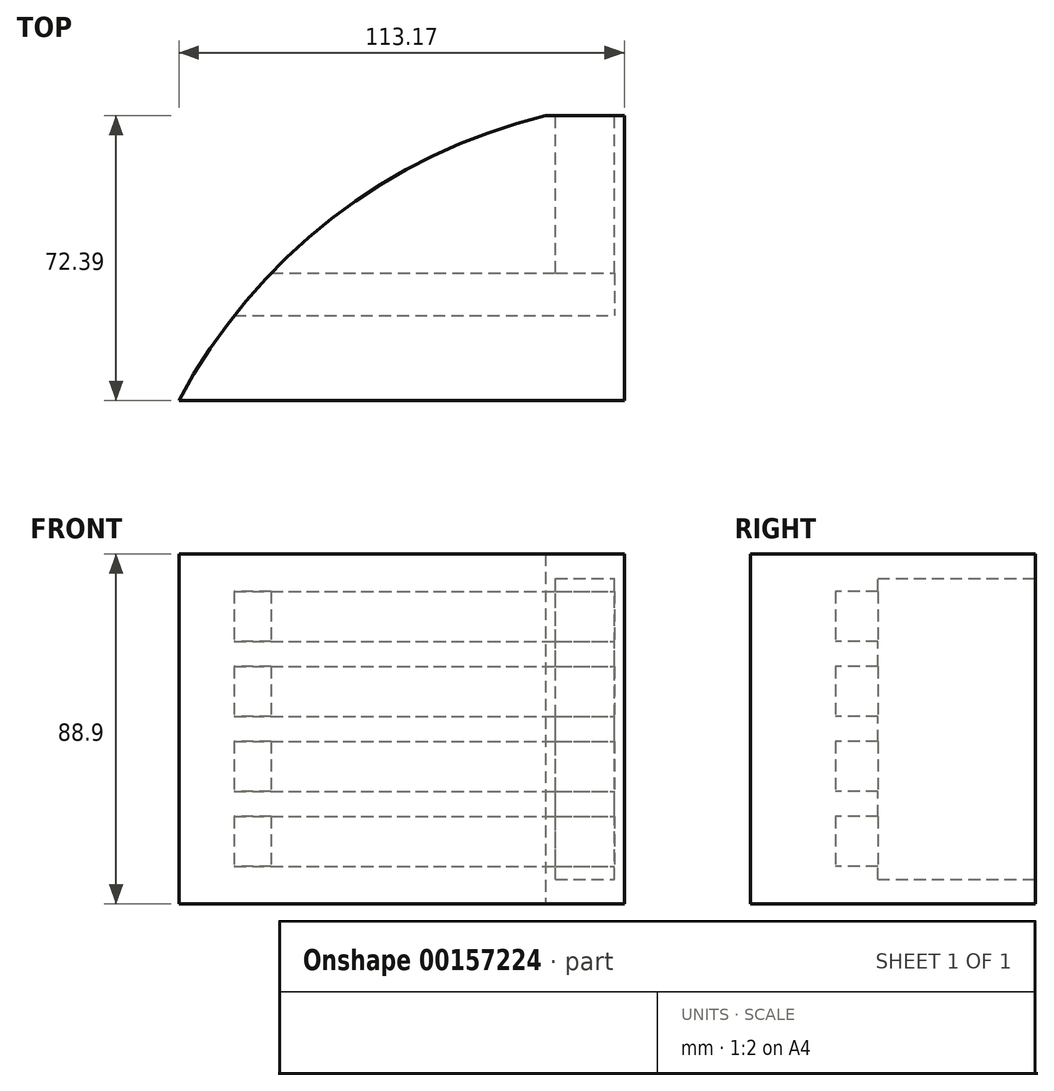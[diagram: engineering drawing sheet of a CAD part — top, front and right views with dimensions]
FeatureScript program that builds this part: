
annotation { "Feature Type Name" : "Feature", "Feature Type Description" : "" }
export const myFeature = defineFeature(function(context is Context, id is Id, definition is map)
    precondition{}
    {
        {
            var Q0;
            Q0=qCreatedBy(makeId("Top.planeOp"),FACE);
            var sketch = newSketch(context, id + "F0", { "sketchPlane" : qUnion([Q0])});
            skLineSegment(sketch, "E0", {"start": v(-50.05, -32.21) * mm, "end": v(43.12, -32.21) * mm});
            skLineSegment(sketch, "E1", {"start": v(43.12, -32.21) * mm, "end": v(43.12, 40.18) * mm});
            skArc(sketch, "E2", {"start": v(43.12, 40.18) * mm, "mid": v(-11.24, 14) * mm, "end": v(-50.05, -32.21) * mm});
            skSolve(sketch);
        }
        {
            var Q0;
            Q0 = qSketchRegion(id + "F0", true);
            extrude(context, id + "F1", {"entities" : qUnion([Q0]), "depth" : 88.9 * mm});
        }
        {
            var Q0;
            Q0=makeQuery(id+"F1.opExtrude","SWEPT_FACE",FACE,{"disambiguationData":[OSD([sQuery(id+"F0.wireOp",EDGE,"E1")])]});
            var sketch = newSketch(context, id + "F2", { "sketchPlane" : qUnion([Q0])});
            skSolve(sketch);
        }
        {
            var Q0;
            {var subQ0=sQuery(id+"F0.wireOp",EDGE,"E1");Q0=makeQuery(id+"F2.imprint","IMPRINT",FACE,{"disambiguationData":[TD([[makeQuery(id+"F2.imprint","IMPRINT",EDGE,{"derivedFrom":makeQuery(id+"F1.opExtrude","CAP_EDGE",EDGE,{"disambiguationData":[OSD([subQ0])],"isStart":true})}),1.0]])]});}
            var sketch = newSketch(context, id + "F3", { "sketchPlane" : qUnion([Q0])});
            skPoint(sketch, "E3.0", {"position": v(40.18, 88.9) * mm});
            skPoint(sketch, "E4.0", {"position": v(-32.21, 0) * mm});
            skLineSegment(sketch, "E5.bottom", {"start": v(40.18, 88.9) * mm, "end": v(-32.21, 88.9) * mm});
            skLineSegment(sketch, "E5.top", {"start": v(40.18, 0) * mm, "end": v(-32.21, 0) * mm});
            skLineSegment(sketch, "E5.left", {"start": v(40.18, 88.9) * mm, "end": v(40.18, 0) * mm});
            skLineSegment(sketch, "E5.right", {"start": v(-32.21, 88.9) * mm, "end": v(-32.21, 0) * mm});
            skSolve(sketch);
        }
        {
            var Q0;
            Q0 = qSketchRegion(id + "F3", true);
            extrude(context, id + "F4", {"entities" : qUnion([Q0]), "operationType" : NewBodyOperationType.ADD, "depth" : 20 * mm});
        }
        {
            var Q0;
            Q0=makeQuery(id+"F4.opExtrude","SWEPT_FACE",FACE,{"disambiguationData":[OSD([sQuery(id+"F3.wireOp",EDGE,"E5.left")])]});
            var sketch = newSketch(context, id + "F5", { "sketchPlane" : qUnion([Q0])});
            skPoint(sketch, "E6.0", {"position": v(-53.12, 0) * mm});
            skPoint(sketch, "E7.0", {"position": v(-53.12, 88.9) * mm});
            skLineSegment(sketch, "E8.bottom", {"start": v(-45.62, 6.2) * mm, "end": v(-60.62, 6.2) * mm});
            skLineSegment(sketch, "E8.top", {"start": v(-45.62, 82.7) * mm, "end": v(-60.62, 82.7) * mm});
            skLineSegment(sketch, "E8.left", {"start": v(-45.62, 6.2) * mm, "end": v(-45.62, 82.7) * mm});
            skLineSegment(sketch, "E8.right", {"start": v(-60.62, 6.2) * mm, "end": v(-60.62, 82.7) * mm});
            skLineSegment(sketch, "E9.0", {"start": v(-63.12, 88.9) * mm, "end": v(-63.12, 0) * mm});
            skSolve(sketch);
        }
        {
            var Q0;
            Q0 = qSketchRegion(id + "F5", true);
            extrude(context, id + "F6", {"entities" : qUnion([Q0]), "operationType" : NewBodyOperationType.REMOVE, "oppositeDirection" : true, "depth" : 40 * mm});
        }
        {
            var Q0;
            Q0=makeQuery(id+"F6.boolean.opBoolean","COPY",FACE,{"derivedFrom":makeQuery(id+"F6.opExtrude","SWEPT_FACE",FACE,{"disambiguationData":[OSD([sQuery(id+"F5.wireOp",EDGE,"E8.right")])]})});
            var sketch = newSketch(context, id + "F7", { "sketchPlane" : qUnion([Q0])});
            skLineSegment(sketch, "E10.0", {"start": v(-0.18, 82.7) * mm, "end": v(-40.18, 82.7) * mm});
            skLineSegment(sketch, "E10.1", {"start": v(-0.18, 6.2) * mm, "end": v(-40.18, 6.2) * mm});
            skLineSegment(sketch, "E10.2", {"start": v(-0.18, 6.2) * mm, "end": v(-0.18, 82.7) * mm});
            skLineSegment(sketch, "E10.3", {"start": v(-40.18, 6.2) * mm, "end": v(-40.18, 82.7) * mm});
            skLineSegment(sketch, "E11.bottom", {"start": v(-40.18, 60.3) * mm, "end": v(10.62, 60.3) * mm});
            skLineSegment(sketch, "E11.top", {"start": v(-40.18, 47.6) * mm, "end": v(10.62, 47.6) * mm});
            skLineSegment(sketch, "E11.left", {"start": v(-40.18, 60.3) * mm, "end": v(-40.18, 47.6) * mm});
            skLineSegment(sketch, "E11.right", {"start": v(10.62, 60.3) * mm, "end": v(10.62, 47.6) * mm});
            skLineSegment(sketch, "E12.bottom", {"start": v(-40.18, 41.25) * mm, "end": v(10.62, 41.25) * mm});
            skLineSegment(sketch, "E12.top", {"start": v(-40.18, 28.55) * mm, "end": v(10.62, 28.55) * mm});
            skLineSegment(sketch, "E12.left", {"start": v(-40.18, 41.25) * mm, "end": v(-40.18, 28.55) * mm});
            skLineSegment(sketch, "E12.right", {"start": v(10.62, 41.25) * mm, "end": v(10.62, 28.55) * mm});
            skLineSegment(sketch, "E13.bottom", {"start": v(-40.18, 22.2) * mm, "end": v(10.62, 22.2) * mm});
            skLineSegment(sketch, "E13.top", {"start": v(-40.18, 9.5) * mm, "end": v(10.62, 9.5) * mm});
            skLineSegment(sketch, "E13.left", {"start": v(-40.18, 22.2) * mm, "end": v(-40.18, 9.5) * mm});
            skLineSegment(sketch, "E13.right", {"start": v(10.62, 22.2) * mm, "end": v(10.62, 9.5) * mm});
            skLineSegment(sketch, "E14.bottom", {"start": v(-40.18, 79.4) * mm, "end": v(10.62, 79.4) * mm});
            skLineSegment(sketch, "E14.top", {"start": v(-40.18, 66.7) * mm, "end": v(10.62, 66.7) * mm});
            skLineSegment(sketch, "E14.left", {"start": v(-40.18, 79.4) * mm, "end": v(-40.18, 66.7) * mm});
            skLineSegment(sketch, "E14.right", {"start": v(10.62, 79.4) * mm, "end": v(10.62, 66.7) * mm});
            skSolve(sketch);
        }
        {
            var Q0;
            {var subQ5=sQuery(id+"F7.wireOp",EDGE,"E13.right");Q0=makeQuery(id+"F7.imprint","IMPRINT",FACE,{"disambiguationData":[TD([[makeQuery(id+"F7.imprint","IMPRINT",EDGE,{"derivedFrom":subQ5}),-1.0]])]});}
            var Q1;
            {var subQ5=sQuery(id+"F7.wireOp",EDGE,"E12.right");Q1=makeQuery(id+"F7.imprint","IMPRINT",FACE,{"disambiguationData":[TD([[makeQuery(id+"F7.imprint","IMPRINT",EDGE,{"derivedFrom":subQ5}),-1.0]])]});}
            var Q2;
            {var subQ5=sQuery(id+"F7.wireOp",EDGE,"E11.right");Q2=makeQuery(id+"F7.imprint","IMPRINT",FACE,{"disambiguationData":[TD([[makeQuery(id+"F7.imprint","IMPRINT",EDGE,{"derivedFrom":subQ5}),-1.0]])]});}
            var Q3;
            {var subQ5=sQuery(id+"F7.wireOp",EDGE,"E14.right");Q3=makeQuery(id+"F7.imprint","IMPRINT",FACE,{"disambiguationData":[TD([[makeQuery(id+"F7.imprint","IMPRINT",EDGE,{"derivedFrom":subQ5}),-1.0]])]});}
            var Q4;
            {var subQ5=sQuery(id+"F7.wireOp",EDGE,"E13.left");Q4=makeQuery(id+"F7.imprint","IMPRINT",FACE,{"disambiguationData":[TD([[makeQuery(id+"F7.imprint","IMPRINT",EDGE,{"derivedFrom":subQ5}),-1.0]])]});}
            var Q5;
            {var subQ5=sQuery(id+"F7.wireOp",EDGE,"E12.left");Q5=makeQuery(id+"F7.imprint","IMPRINT",FACE,{"disambiguationData":[TD([[makeQuery(id+"F7.imprint","IMPRINT",EDGE,{"derivedFrom":subQ5}),-1.0]])]});}
            var Q6;
            {var subQ5=sQuery(id+"F7.wireOp",EDGE,"E11.left");Q6=makeQuery(id+"F7.imprint","IMPRINT",FACE,{"disambiguationData":[TD([[makeQuery(id+"F7.imprint","IMPRINT",EDGE,{"derivedFrom":subQ5}),-1.0]])]});}
            var Q7;
            {var subQ5=sQuery(id+"F7.wireOp",EDGE,"E14.left");Q7=makeQuery(id+"F7.imprint","IMPRINT",FACE,{"disambiguationData":[TD([[makeQuery(id+"F7.imprint","IMPRINT",EDGE,{"derivedFrom":subQ5}),-1.0]])]});}
            extrude(context, id + "F8", {"entities" : qUnion([Q0, Q1, Q2, Q3, Q4, Q5, Q6, Q7]), "operationType" : NewBodyOperationType.REMOVE, "endBound" : BoundingType.THROUGH_ALL, "depth" : 25.4 * mm});
        }
    });
